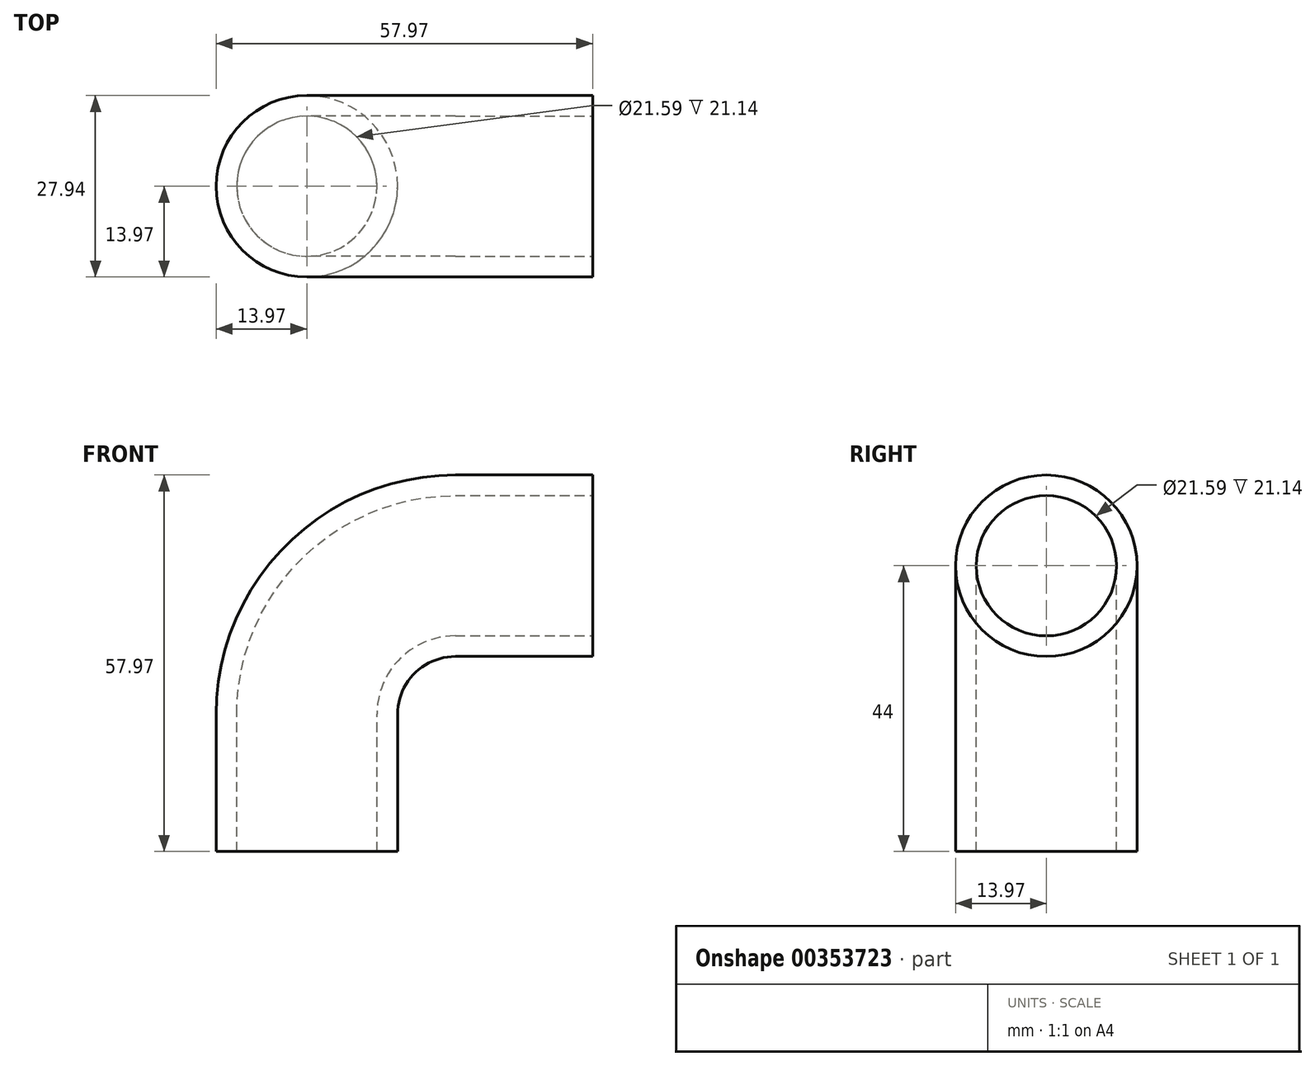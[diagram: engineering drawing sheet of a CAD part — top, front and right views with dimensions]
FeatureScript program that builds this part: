
annotation { "Feature Type Name" : "Feature", "Feature Type Description" : "" }
export const myFeature = defineFeature(function(context is Context, id is Id, definition is map)
    precondition{}
    {
        {
            var Q0;
            Q0=qCreatedBy(makeId("Front.planeOp"),FACE);
            var sketch = newSketch(context, id + "F0", { "sketchPlane" : qUnion([Q0])});
            skLineSegment(sketch, "E0", {"start": v(0, 0) * mm, "end": v(0, 21.14) * mm});
            skLineSegment(sketch, "E1", {"start": v(22.86, 44) * mm, "end": v(44, 44) * mm});
            skPoint(sketch, "E2.visualSharp", {"position": v(0, 44) * mm});
            skArc(sketch, "E2.filletArc", {"start": v(22.86, 44) * mm, "mid": v(6.7, 37.3) * mm, "end": v(0, 21.14) * mm});
            skSolve(sketch);
        }
        {
            var Q0;
            Q0=qCreatedBy(makeId("Top.planeOp"),FACE);
            var sketch = newSketch(context, id + "F1", { "sketchPlane" : qUnion([Q0])});
            skCircle(sketch, "E3", {"center": v(0, 0) * mm, "radius": 13.97 * mm});
            skSolve(sketch);
        }
        {
            var Q0;
            Q0 = qSketchRegion(id + "F1", true);
            var Q1;
            Q1 = qConstructionFilter(qBodyType(qCreatedBy(id + "F0" ,EDGE), BodyType.WIRE), ConstructionObject.NO);
            sweep(context, id + "F2", {"profiles" : qUnion([Q0]), "path" : qUnion([Q1])});
        }
        {
            var Q0;
            Q0=makeQuery(id+"F2.opSweep","CAP_FACE",FACE,{"disambiguationData":[OSD([sQuery(id+"F0.wireOp",VERTEX,"E0.start"),sQuery(id+"F1.wireOp",EDGE,"E3")])],"isStart":true});
            var sketch = newSketch(context, id + "F3", { "sketchPlane" : qUnion([Q0])});
            skCircle(sketch, "E4", {"center": v(0, 0) * mm, "radius": 10.8 * mm});
            skSolve(sketch);
        }
        {
            var Q0;
            Q0 = qSketchRegion(id + "F3", true);
            var Q1;
            Q1 = qConstructionFilter(qBodyType(qCreatedBy(id + "F0" ,EDGE), BodyType.WIRE), ConstructionObject.NO);
            sweep(context, id + "F4", {"operationType" : NewBodyOperationType.REMOVE, "profiles" : qUnion([Q0]), "path" : qUnion([Q1])});
        }
    });
